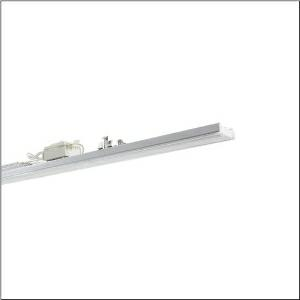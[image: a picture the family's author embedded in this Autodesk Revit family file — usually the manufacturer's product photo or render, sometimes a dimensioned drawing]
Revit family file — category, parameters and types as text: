
# Revit family: licross_r__11_recessed_mo_51te19dn495g_a71c
name_source: partatom
category: Lighting Fixtures
units: mm (PartAtom-declared; Revit-internal decimal feet)

## family parameters
Cut with Voids When Loaded = No
Host = Face
Light Source = No
Part Type = Normal
Room Calculation Point = No
Round Connector Dimension = Use Diameter
Shared = No

## types (1)
- --- (1 x LED, 9810 lm, 56.7 W, 4000K)
    Apparent Load = 57 VA
    CIE Flux Codes = 55 90 98 100 100
    Color Rendering = 80
    Color Temperature = 4000K
    Default Elevation = 1800 mm
    Description = Licross® 11 Recessed MO, luminaire insert, of sheet steel, galvanised, coil coated, white, length: 1.500mm, width: 66mm, height: 67mm, LED rated luminous flux: 9.810lm, light colour: 840, control gear: DALI 2, with plug, 5-pole, with phase selection, mains connection: 220..240V, AC, 50/60Hz, rated input power: 57W, halogen-free wiring, primary light control with lens, of plastic, primary optical cover: cover, of PMMA, light emission: direct distribution, primary light characteristic: double asymmetric, protection rating (complete): IP54, insulation class (complete): insulation class I (protective earthing), certification: CE, ENEC, VDE, UKCA, protection symbol: D if used in an environment with non-conductive dust loads with corresponding accessories, impact resistance: IK06, permissible ambient temperature for indoor applications: -25..+35°C, corresponds to IFS (International Featured Standards) requirements for safety and quality in the food industry, reducing of maximum allowable ambient temperature of 5°C with ceiling mounting, LABS conformity tested according to VDMA 24364:2018-05, packaging unit: 1 piece
    Height = 58 mm
    Lamp = 1 x LED
    Lamp Light Flux = 9810 lm
    Lamp Power = 56.7 W
    Lamp count = 1
    Length = 1500 mm
    Luminous efficacy = 173 lm/W
    Manufacturer = Siteco
    ModVariant = No
    Model = 51TE19DN495G
    Mounting Place = Ceiling
    Mounting Type = Pendant
    Number of Poles = 1
    OnlyDefault = Yes
    Power Factor = 1
    Product Name = Licross® 11 Recessed MO
    Product group = luminaire insert
    ProductGroupID = 902
    Protection Class = Protection class I
    Protection Degree = IP 54
    RLX_Detail_Level = 1
    RLX_Emergency_Light_Flux = 0 lm
    RLX_Emergency_Type = 0
    RLX_Emergency_Type_DB = No
    RlxData = <blob elided: 24513 chars, md5=fd8b81b1>
    Socket = socket
    Standby Power = 0 W
    System Light Flux = 9810 lm
    System Power = 57 W
    Type Comments = factory setting: luminous flux: 100 % | dim-lin: 254 | 378 mA
    Type Image = l_1296930.jpg
    URL = http://relux.com
    VarID = @adj_100804
    Voltage = 0 V
    Weight = 0.00 kg
    Width = 66 mm

## geometry (parser evidence)
native form markers: Blend x4, Sweep x10
no freeform markers — native parametric forms only
